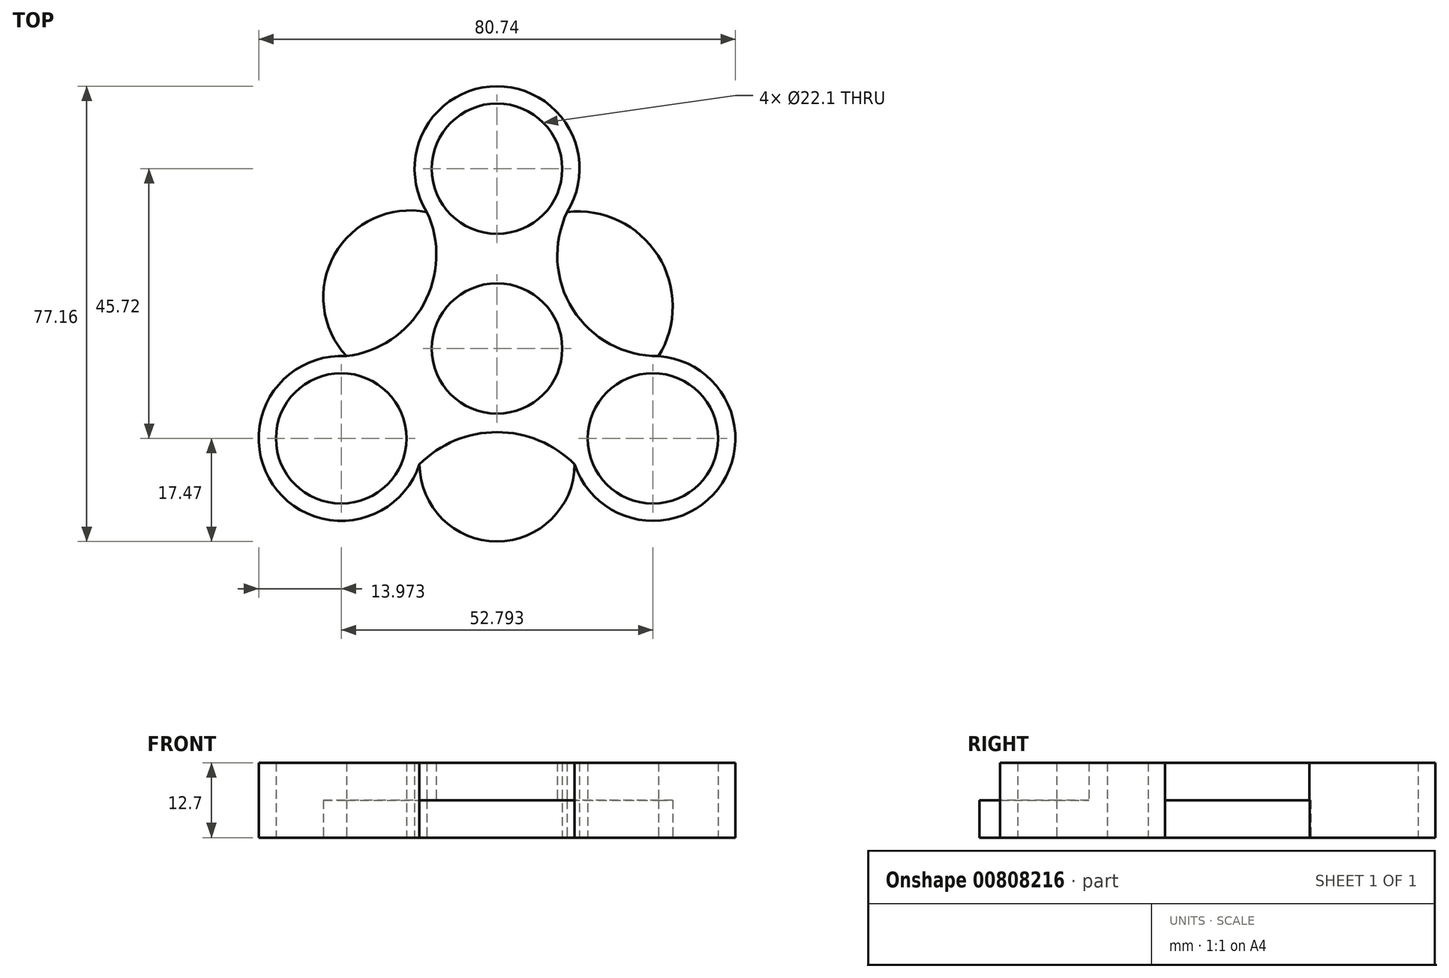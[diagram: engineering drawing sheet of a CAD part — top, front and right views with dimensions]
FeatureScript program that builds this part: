
annotation { "Feature Type Name" : "Feature", "Feature Type Description" : "" }
export const myFeature = defineFeature(function(context is Context, id is Id, definition is map)
    precondition{}
    {
        {
            var Q0;
            Q0=qCreatedBy(makeId("Top.planeOp"),FACE);
            var sketch = newSketch(context, id + "F0", { "sketchPlane" : qUnion([Q0])});
            skCircle(sketch, "E0", {"center": v(0, 0) * mm, "radius": 11.05 * mm});
            skCircle(sketch, "E1", {"center": v(0, 30.48) * mm, "radius": 11.05 * mm});
            skCircle(sketch, "E2.1.0", {"center": v(-26.4, -15.24) * mm, "radius": 11.05 * mm});
            skCircle(sketch, "E2.2.0", {"center": v(26.4, -15.24) * mm, "radius": 11.05 * mm});
            skCircle(sketch, "E3", {"center": v(0, 30.48) * mm, "radius": 13.97 * mm});
            skCircle(sketch, "E4", {"center": v(-26.4, -15.24) * mm, "radius": 13.97 * mm});
            skCircle(sketch, "E5", {"center": v(26.4, -15.24) * mm, "radius": 13.97 * mm});
            skCircle(sketch, "E6", {"center": v(0, 0) * mm, "radius": 13.97 * mm});
            skArc(sketch, "E7", {"start": v(13.14, -19.65) * mm, "mid": v(0, -14.18) * mm, "end": v(-13.13, -19.63) * mm});
            skArc(sketch, "E8", {"start": v(11.88, 23.13) * mm, "mid": v(12.85, 6.63) * mm, "end": v(27.36, -1.3) * mm});
            skArc(sketch, "E9", {"start": v(-25.51, -1.3) * mm, "mid": v(-12.47, 7.44) * mm, "end": v(-11.88, 23.13) * mm});
            skArc(sketch, "E10", {"start": v(-13.13, -19.63) * mm, "mid": v(0, -32.7) * mm, "end": v(13.14, -19.65) * mm});
            skArc(sketch, "E11", {"start": v(27.36, -1.3) * mm, "mid": v(27.26, 15.75) * mm, "end": v(11.88, 23.13) * mm});
            skArc(sketch, "E12", {"start": v(-11.88, 23.13) * mm, "mid": v(-27.56, 15.86) * mm, "end": v(-25.51, -1.3) * mm});
            skSolve(sketch);
        }
        {
            var Q0;
            Q0=makeQuery(id+"F0.imprint","IMPRINT",FACE,{"disambiguationData":[TD([[makeQuery(id+"F0.imprint","IMPRINT",EDGE,{"derivedFrom":sQuery(id+"F0.wireOp",EDGE,"E2.2.0")}),1.0]])]});
            var Q1;
            Q1=makeQuery(id+"F0.imprint","IMPRINT",FACE,{"disambiguationData":[TD([[makeQuery(id+"F0.imprint","IMPRINT",EDGE,{"derivedFrom":sQuery(id+"F0.wireOp",EDGE,"E0")}),-1.0]])]});
            var Q2;
            Q2=makeQuery(id+"F0.imprint","IMPRINT",FACE,{"disambiguationData":[TD([[makeQuery(id+"F0.imprint","IMPRINT",EDGE,{"derivedFrom":sQuery(id+"F0.wireOp",EDGE,"E0")}),1.0]])]});
            var Q3;
            Q3=makeQuery(id+"F0.imprint","IMPRINT",FACE,{"disambiguationData":[TD([[makeQuery(id+"F0.imprint","IMPRINT",EDGE,{"derivedFrom":sQuery(id+"F0.wireOp",EDGE,"E2.2.0")}),-1.0]])]});
            var Q4;
            Q4=makeQuery(id+"F0.imprint","IMPRINT",FACE,{"disambiguationData":[TD([[makeQuery(id+"F0.imprint","IMPRINT",EDGE,{"derivedFrom":sQuery(id+"F0.wireOp",EDGE,"E1")}),-1.0]])]});
            var Q5;
            Q5=makeQuery(id+"F0.imprint","IMPRINT",FACE,{"disambiguationData":[TD([[makeQuery(id+"F0.imprint","IMPRINT",EDGE,{"derivedFrom":sQuery(id+"F0.wireOp",EDGE,"E6")}),-1.0]])]});
            var Q6;
            Q6=makeQuery(id+"F0.imprint","IMPRINT",FACE,{"disambiguationData":[TD([[makeQuery(id+"F0.imprint","IMPRINT",EDGE,{"derivedFrom":sQuery(id+"F0.wireOp",EDGE,"E1")}),1.0]])]});
            var Q7;
            {var subQ0=sQuery(id+"F0.wireOp",EDGE,"E8");var subQ1=sQuery(id+"F0.wireOp",EDGE,"E5");var subQ2=makeQuery(id+"F0.imprint","INTERSECT",VERTEX,{"disambiguationData":[OD(0.0)],"derivedFrom":[subQ1,subQ0]});Q7=makeQuery(id+"F0.imprint","IMPRINT",FACE,{"disambiguationData":[TD([[makeQuery(id+"F0.imprint","IMPRINT",EDGE,{"disambiguationData":[TD([[subQ2,-1.0]])],"derivedFrom":subQ1}),1.0]])]});}
            var Q8;
            Q8=makeQuery(id+"F0.imprint","IMPRINT",FACE,{"disambiguationData":[TD([[makeQuery(id+"F0.imprint","IMPRINT",EDGE,{"derivedFrom":sQuery(id+"F0.wireOp",EDGE,"E2.1.0")}),-1.0]])]});
            var Q9;
            Q9=makeQuery(id+"F0.imprint","IMPRINT",FACE,{"disambiguationData":[TD([[makeQuery(id+"F0.imprint","IMPRINT",EDGE,{"derivedFrom":sQuery(id+"F0.wireOp",EDGE,"E2.1.0")}),1.0]])]});
            extrude(context, id + "F1", {"entities" : qUnion([Q0, Q1, Q2, Q3, Q4, Q5, Q6, Q7, Q8, Q9]), "depth" : 6.35 * mm, "offsetDistance" : 25.4 * mm});
        }
        {
            var Q0;
            Q0=makeQuery(id+"F1.opExtrude","CAP_FACE",FACE,{"disambiguationData":[OSD([sQuery(id+"F0.wireOp",EDGE,"E3"),sQuery(id+"F0.wireOp",EDGE,"E4"),sQuery(id+"F0.wireOp",EDGE,"E5"),sQuery(id+"F0.wireOp",EDGE,"E7"),sQuery(id+"F0.wireOp",EDGE,"E8"),sQuery(id+"F0.wireOp",EDGE,"E9")])],"isStart":false});
            var sketch = newSketch(context, id + "F2", { "sketchPlane" : qUnion([Q0])});
            skCircle(sketch, "E13", {"center": v(0, 30.48) * mm, "radius": 11.05 * mm});
            skCircle(sketch, "E14", {"center": v(26.4, -15.24) * mm, "radius": 11.05 * mm});
            skCircle(sketch, "E15", {"center": v(-26.4, -15.24) * mm, "radius": 11.05 * mm});
            skCircle(sketch, "E16", {"center": v(0, 0) * mm, "radius": 11.05 * mm});
            skSolve(sketch);
        }
        {
            var Q0;
            Q0=makeQuery(id+"F2.imprint","IMPRINT",FACE,{"disambiguationData":[TD([[makeQuery(id+"F2.imprint","IMPRINT",EDGE,{"derivedFrom":sQuery(id+"F2.wireOp",EDGE,"E15")}),1.0]])]});
            var Q1;
            Q1=makeQuery(id+"F2.imprint","IMPRINT",FACE,{"disambiguationData":[TD([[makeQuery(id+"F2.imprint","IMPRINT",EDGE,{"derivedFrom":sQuery(id+"F2.wireOp",EDGE,"E13")}),1.0]])]});
            var Q2;
            Q2=makeQuery(id+"F2.imprint","IMPRINT",FACE,{"disambiguationData":[TD([[makeQuery(id+"F2.imprint","IMPRINT",EDGE,{"derivedFrom":sQuery(id+"F2.wireOp",EDGE,"E14")}),1.0]])]});
            extrude(context, id + "F3", {"entities" : qUnion([Q0, Q1, Q2]), "operationType" : NewBodyOperationType.REMOVE, "oppositeDirection" : true, "depth" : 6.35 * mm, "offsetDistance" : 25.4 * mm});
        }
        {
            var Q0;
            Q0=makeQuery(id+"F2.imprint","IMPRINT",FACE,{"disambiguationData":[TD([[makeQuery(id+"F2.imprint","IMPRINT",EDGE,{"derivedFrom":sQuery(id+"F2.wireOp",EDGE,"E16")}),1.0]])]});
            extrude(context, id + "F4", {"entities" : qUnion([Q0]), "operationType" : NewBodyOperationType.REMOVE, "oppositeDirection" : true, "depth" : 6.35 * mm, "offsetDistance" : 25.4 * mm});
        }
        {
            var Q0;
            Q0=makeQuery(id+"F0.imprint","IMPRINT",FACE,{"disambiguationData":[TD([[makeQuery(id+"F0.imprint","IMPRINT",EDGE,{"derivedFrom":sQuery(id+"F0.wireOp",EDGE,"E9")}),1.0]])]});
            var Q1;
            {var subQ0=sQuery(id+"F0.wireOp",EDGE,"E11");Q1=makeQuery(id+"F0.imprint","IMPRINT",FACE,{"disambiguationData":[TD([[makeQuery(id+"F0.imprint","IMPRINT",EDGE,{"derivedFrom":subQ0}),1.0]])]});}
            var Q2;
            Q2=makeQuery(id+"F0.imprint","IMPRINT",FACE,{"disambiguationData":[TD([[makeQuery(id+"F0.imprint","IMPRINT",EDGE,{"derivedFrom":sQuery(id+"F0.wireOp",EDGE,"E7")}),1.0]])]});
            var Q3;
            Q3=makeQuery(id+"F0.imprint","IMPRINT",FACE,{"disambiguationData":[TD([[makeQuery(id+"F0.imprint","IMPRINT",EDGE,{"derivedFrom":sQuery(id+"F0.wireOp",EDGE,"E2.2.0")}),1.0]])]});
            var Q4;
            Q4=makeQuery(id+"F0.imprint","IMPRINT",FACE,{"disambiguationData":[TD([[makeQuery(id+"F0.imprint","IMPRINT",EDGE,{"derivedFrom":sQuery(id+"F0.wireOp",EDGE,"E1")}),1.0]])]});
            var Q5;
            Q5=makeQuery(id+"F0.imprint","IMPRINT",FACE,{"disambiguationData":[TD([[makeQuery(id+"F0.imprint","IMPRINT",EDGE,{"derivedFrom":sQuery(id+"F0.wireOp",EDGE,"E2.1.0")}),1.0]])]});
            var Q6;
            Q6=makeQuery(id+"F0.imprint","IMPRINT",FACE,{"disambiguationData":[TD([[makeQuery(id+"F0.imprint","IMPRINT",EDGE,{"derivedFrom":sQuery(id+"F0.wireOp",EDGE,"E0")}),1.0]])]});
            var Q7;
            Q7=makeQuery(id+"F1.opExtrude","CAP_FACE",FACE,{"disambiguationData":[OSD([sQuery(id+"F0.wireOp",EDGE,"E3"),sQuery(id+"F0.wireOp",EDGE,"E4"),sQuery(id+"F0.wireOp",EDGE,"E5"),sQuery(id+"F0.wireOp",EDGE,"E7"),sQuery(id+"F0.wireOp",EDGE,"E8"),sQuery(id+"F0.wireOp",EDGE,"E9")])],"isStart":false});
            var Q8;
            Q8=makeQuery(id+"F0.imprint","IMPRINT",FACE,{"disambiguationData":[TD([[makeQuery(id+"F0.imprint","IMPRINT",EDGE,{"derivedFrom":sQuery(id+"F0.wireOp",EDGE,"E1")}),-1.0]])]});
            var Q9;
            Q9=makeQuery(id+"F0.imprint","IMPRINT",FACE,{"disambiguationData":[TD([[makeQuery(id+"F0.imprint","IMPRINT",EDGE,{"derivedFrom":sQuery(id+"F0.wireOp",EDGE,"E0")}),-1.0]])]});
            var Q10;
            Q10=makeQuery(id+"F0.imprint","IMPRINT",FACE,{"disambiguationData":[TD([[makeQuery(id+"F0.imprint","IMPRINT",EDGE,{"derivedFrom":sQuery(id+"F0.wireOp",EDGE,"E2.1.0")}),-1.0]])]});
            var Q11;
            Q11=makeQuery(id+"F0.imprint","IMPRINT",FACE,{"disambiguationData":[TD([[makeQuery(id+"F0.imprint","IMPRINT",EDGE,{"derivedFrom":sQuery(id+"F0.wireOp",EDGE,"E6")}),-1.0]])]});
            var Q12;
            Q12=makeQuery(id+"F0.imprint","IMPRINT",FACE,{"disambiguationData":[TD([[makeQuery(id+"F0.imprint","IMPRINT",EDGE,{"derivedFrom":sQuery(id+"F0.wireOp",EDGE,"E2.2.0")}),-1.0]])]});
            var Q13;
            Q13=makeQuery(id+"F1.opExtrude","CAP_FACE",FACE,{"disambiguationData":[OSD([sQuery(id+"F0.wireOp",EDGE,"E3"),sQuery(id+"F0.wireOp",EDGE,"E4"),sQuery(id+"F0.wireOp",EDGE,"E5"),sQuery(id+"F0.wireOp",EDGE,"E7"),sQuery(id+"F0.wireOp",EDGE,"E8"),sQuery(id+"F0.wireOp",EDGE,"E9")])],"isStart":true});
            var Q14;
            {var subQ0=sQuery(id+"F0.wireOp",EDGE,"E8");var subQ1=sQuery(id+"F0.wireOp",EDGE,"E5");var subQ3=makeQuery(id+"F0.imprint","INTERSECT",VERTEX,{"derivedFrom":[subQ1,subQ0]});Q14=makeQuery(id+"F0.imprint","IMPRINT",FACE,{"disambiguationData":[TD([[makeQuery(id+"F0.imprint","IMPRINT",EDGE,{"disambiguationData":[TD([[subQ3,1.0]])],"derivedFrom":subQ1}),1.0]])]});}
            extrude(context, id + "F5", {"entities" : qUnion([Q0, Q1, Q2, Q3, Q4, Q5, Q6, Q7, Q8, Q9, Q10, Q11, Q12, Q13, Q14]), "operationType" : NewBodyOperationType.ADD, "depth" : 6.35 * mm, "offsetDistance" : 25.4 * mm});
        }
        {
            var Q0;
            Q0=makeQuery(id+"F2.imprint","IMPRINT",FACE,{"disambiguationData":[TD([[makeQuery(id+"F2.imprint","IMPRINT",EDGE,{"derivedFrom":sQuery(id+"F2.wireOp",EDGE,"E15")}),1.0]])]});
            var Q1;
            Q1=makeQuery(id+"F2.imprint","IMPRINT",FACE,{"disambiguationData":[TD([[makeQuery(id+"F2.imprint","IMPRINT",EDGE,{"derivedFrom":sQuery(id+"F2.wireOp",EDGE,"E16")}),1.0]])]});
            var Q2;
            Q2=makeQuery(id+"F2.imprint","IMPRINT",FACE,{"disambiguationData":[TD([[makeQuery(id+"F2.imprint","IMPRINT",EDGE,{"derivedFrom":sQuery(id+"F2.wireOp",EDGE,"E13")}),1.0]])]});
            var Q3;
            Q3=makeQuery(id+"F2.imprint","IMPRINT",FACE,{"disambiguationData":[TD([[makeQuery(id+"F2.imprint","IMPRINT",EDGE,{"derivedFrom":sQuery(id+"F2.wireOp",EDGE,"E14")}),1.0]])]});
            extrude(context, id + "F6", {"entities" : qUnion([Q0, Q1, Q2, Q3]), "operationType" : NewBodyOperationType.REMOVE, "oppositeDirection" : true, "depth" : 25.4 * mm, "offsetDistance" : 25.4 * mm});
        }
    });
